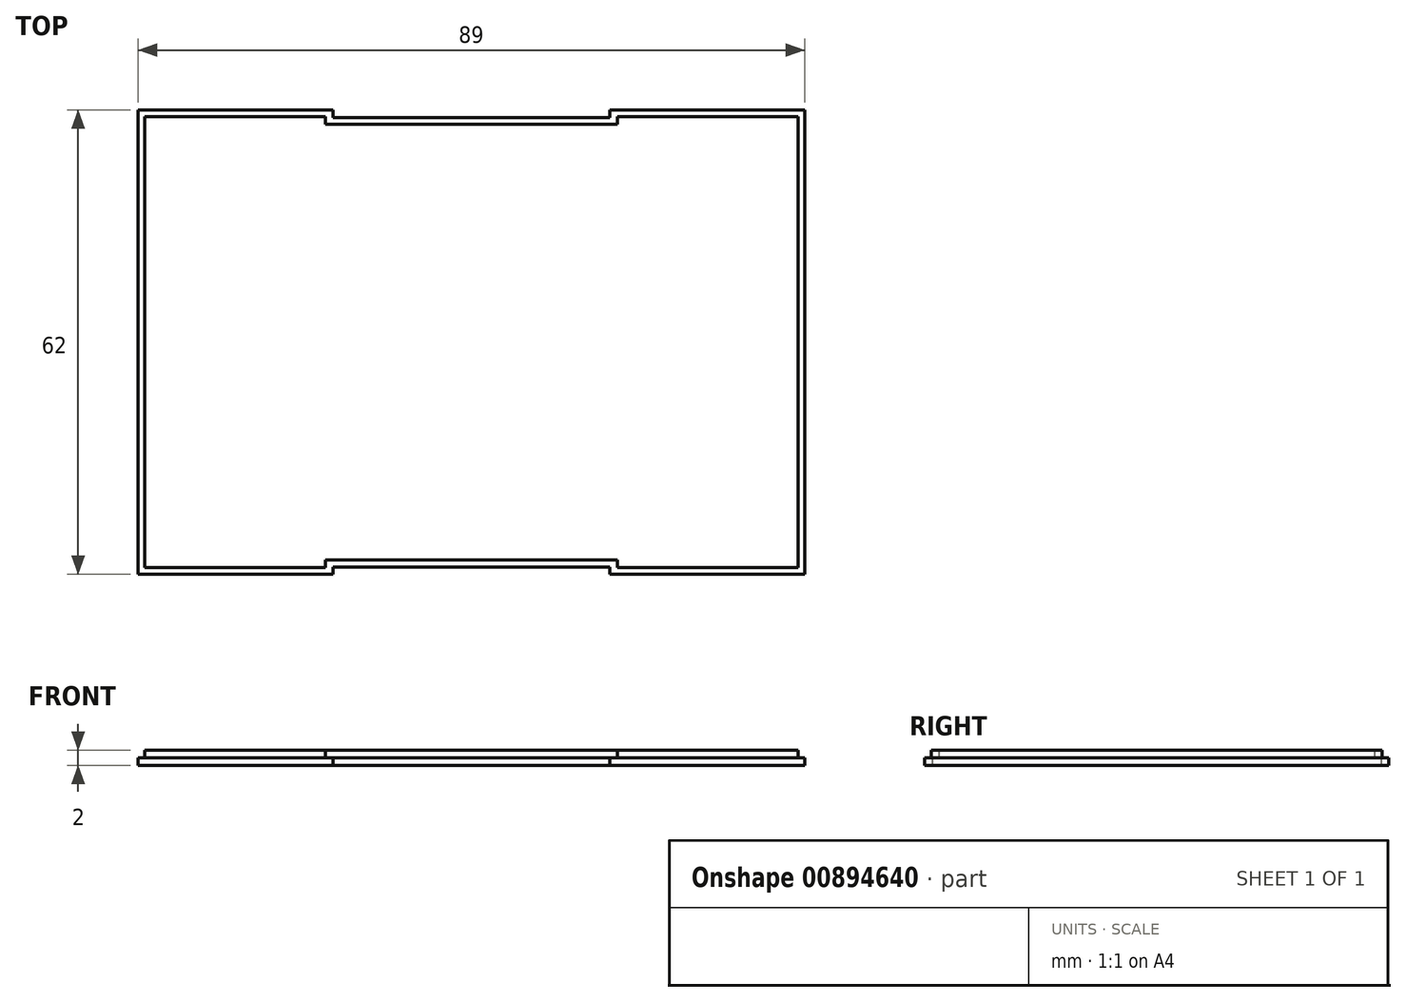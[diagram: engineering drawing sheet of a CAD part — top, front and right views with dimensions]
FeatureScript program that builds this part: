
annotation { "Feature Type Name" : "Feature", "Feature Type Description" : "" }
export const myFeature = defineFeature(function(context is Context, id is Id, definition is map)
    precondition{}
    {
        {
            var Q0;
            Q0=qCreatedBy(makeId("Top.planeOp"),FACE);
            var sketch = newSketch(context, id + "F0", { "sketchPlane" : qUnion([Q0])});
            skLineSegment(sketch, "E0.bottom", {"start": v(44.5, -30) * mm, "end": v(-44.5, -30) * mm});
            skLineSegment(sketch, "E0.top", {"start": v(44.5, 30) * mm, "end": v(-44.5, 30) * mm});
            skLineSegment(sketch, "E0.left", {"start": v(44.5, -30) * mm, "end": v(44.5, 30) * mm});
            skLineSegment(sketch, "E0.right", {"start": v(-44.5, -30) * mm, "end": v(-44.5, 30) * mm});
            skPoint(sketch, "E0.middle", {"position": v(0, 0) * mm});
            skLineSegment(sketch, "E1.bottom", {"start": v(-44.5, 31) * mm, "end": v(-18.5, 31) * mm});
            skLineSegment(sketch, "E1.top", {"start": v(-44.5, -31) * mm, "end": v(-18.5, -31) * mm});
            skLineSegment(sketch, "E1.left", {"start": v(-44.5, 31) * mm, "end": v(-44.5, -31) * mm});
            skLineSegment(sketch, "E1.right", {"start": v(-18.5, 31) * mm, "end": v(-18.5, -31) * mm});
            skLineSegment(sketch, "E2.bottom", {"start": v(18.5, 31) * mm, "end": v(44.5, 31) * mm});
            skLineSegment(sketch, "E2.top", {"start": v(18.5, -31) * mm, "end": v(44.5, -31) * mm});
            skLineSegment(sketch, "E2.left", {"start": v(18.5, 31) * mm, "end": v(18.5, -31) * mm});
            skLineSegment(sketch, "E2.right", {"start": v(44.5, 31) * mm, "end": v(44.5, -31) * mm});
            skSolve(sketch);
        }
        {
            var Q0;
            Q0 = qSketchRegion(id + "F0", true);
            extrude(context, id + "F1", {"entities" : qUnion([Q0]), "depth" : 1 * mm, "offsetDistance" : 25.4 * mm});
        }
        {
            var Q0;
            Q0=makeQuery(id+"F1.opExtrude","CAP_FACE",FACE,{"disambiguationData":[OSD([sQuery(id+"F0.wireOp",EDGE,"E0.bottom"),sQuery(id+"F0.wireOp",EDGE,"E0.top"),sQuery(id+"F0.wireOp",EDGE,"E1.bottom"),sQuery(id+"F0.wireOp",EDGE,"E1.top"),sQuery(id+"F0.wireOp",EDGE,"E1.left"),sQuery(id+"F0.wireOp",EDGE,"E1.right"),sQuery(id+"F0.wireOp",EDGE,"E2.bottom"),sQuery(id+"F0.wireOp",EDGE,"E2.top"),sQuery(id+"F0.wireOp",EDGE,"E2.left"),sQuery(id+"F0.wireOp",EDGE,"E2.right")])],"isStart":false});
            var sketch = newSketch(context, id + "F2", { "sketchPlane" : qUnion([Q0])});
            skLineSegment(sketch, "E3.bottom", {"start": v(-43.6, 30.1) * mm, "end": v(-19.5, 30.1) * mm});
            skLineSegment(sketch, "E3.top", {"start": v(-43.6, -30.1) * mm, "end": v(-19.5, -30.1) * mm});
            skLineSegment(sketch, "E3.left", {"start": v(-43.6, 30.1) * mm, "end": v(-43.6, -30.1) * mm});
            skLineSegment(sketch, "E3.right", {"start": v(-19.5, 30.1) * mm, "end": v(-19.5, -30.1) * mm});
            skLineSegment(sketch, "E4.bottom", {"start": v(19.5, 30.1) * mm, "end": v(43.6, 30.1) * mm});
            skLineSegment(sketch, "E4.top", {"start": v(19.5, -30.1) * mm, "end": v(43.6, -30.1) * mm});
            skLineSegment(sketch, "E4.left", {"start": v(19.5, 30.1) * mm, "end": v(19.5, -30.1) * mm});
            skLineSegment(sketch, "E4.right", {"start": v(43.6, 30.1) * mm, "end": v(43.6, -30.1) * mm});
            skLineSegment(sketch, "E5.bottom", {"start": v(-19.5, 29.1) * mm, "end": v(19.5, 29.1) * mm});
            skLineSegment(sketch, "E5.top", {"start": v(-19.5, -29.1) * mm, "end": v(19.5, -29.1) * mm});
            skLineSegment(sketch, "E5.left", {"start": v(-19.5, 29.1) * mm, "end": v(-19.5, -29.1) * mm});
            skLineSegment(sketch, "E5.right", {"start": v(19.5, 29.1) * mm, "end": v(19.5, -29.1) * mm});
            skSolve(sketch);
        }
        {
            var Q0;
            Q0 = qSketchRegion(id + "F2", true);
            extrude(context, id + "F3", {"entities" : qUnion([Q0]), "operationType" : NewBodyOperationType.ADD, "depth" : 1 * mm, "offsetDistance" : 25.4 * mm});
        }
    });
